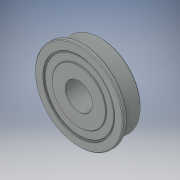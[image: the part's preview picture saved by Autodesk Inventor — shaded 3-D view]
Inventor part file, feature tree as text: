
AUTODESK INVENTOR PART (.ipt)
format: ipt  version: 2018 (Build 220112000, 112)  size: 232,960 bytes
history: native  units: in
note: dims shown in document units (in); Inventor stores cm internally (conversion verified against a paired STEP export)
features: chamfer x1
ambient origin geometry x8: Origin, YZ Plane, XZ Plane, XY Plane, X Axis, Y Axis, Z Axis, Center Point
bodies: Solid1 (feature_tree)
feature tree (1):
  chamfer  "Chamfer7"  [1 undecoded]
note: 1 required parameter value undecoded (feature->parameter linkage not recoverable at this tier; creation-order binding heuristic only, values carry confidence <= 0.55)
